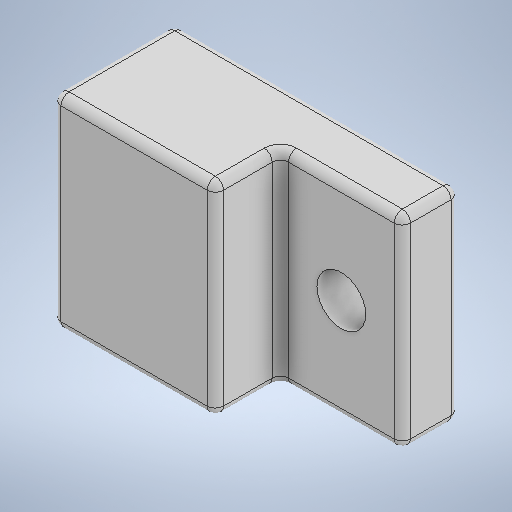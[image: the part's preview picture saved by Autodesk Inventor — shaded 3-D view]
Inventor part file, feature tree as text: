
AUTODESK INVENTOR PART (.ipt)
format: ipt  version: 2025.1 (Build 291241000, 241)  size: 267,776 bytes
history: native  units: mm
features: sketch x7, extrude x4, other x1, fillet x1
ambient origin geometry x8: Origin, YZ Plane, XZ Plane, XY Plane, X Axis, Y Axis, Z Axis, Center Point
bodies: Body1 (feature_tree)
feature tree (13):
  other  "Sólido1"
  extrude  "Extrusión1"  Depth=25.0mm
  extrude  "Extrusión2"  Depth=15.0mm
  fillet  "Empalme1"  Radius=8.0mm
  sketch  "Boceto3"  dims[d7=1.0mm d8=11.5mm]
  sketch  "Boceto4"  dims[d9=6.0mm d10=8.0mm d11=0.0mm]
  sketch  "Boceto5"  dims[d12=6.5mm]
  extrude  "Extrusión3"  Depth=1.0mm
  extrude  "Extrusión4"  Depth=8.0mm TaperAngle=0.0deg
  sketch  "Boceto7"  dims[d14=10.0mm d15=0.0mm]
  sketch  "Boceto1"  dims[d0=35.0mm d1=25.0mm]
  sketch  "Boceto2"  dims[d2=15.0mm d3=0.0mm d4=15.0mm d5=8.0mm d6=0.0mm]
  sketch  "Boceto6"  dims[d13=6.0mm]
